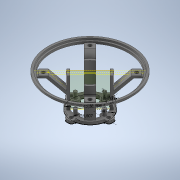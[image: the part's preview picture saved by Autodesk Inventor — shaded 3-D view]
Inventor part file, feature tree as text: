
AUTODESK INVENTOR PART (.ipt)
format: ipt  version: 2020 (Build 240168000, 168)  size: 594,432 bytes
history: native  units: mm
features: projected_geometry x28, sketch x16, extrude x9, other x5, pattern_circular x1, sweep x1
ambient origin geometry x8: Origin, YZ Plane, XZ Plane, XY Plane, X Axis, Y Axis, Z Axis, Center Point
bodies: Body1 (feature_tree)
feature tree (60):
  other  "Твердое тело1"
  sketch  "Эскиз1"
  extrude  "Выдавливание1"  Depth=44.0mm
  extrude  "Выдавливание2"  Depth=4.0mm
  sketch  "Эскиз3"
  extrude  "Выдавливание4"  Depth=40.0mm TaperAngle=360.0deg
  pattern_circular  "Круговой массив1"  [2 undecoded]
  other  "РабПлоскость2"
  sketch  "Эскиз5"
  other  "РабПлоскость1"
  sketch  "Эскиз6"
  sketch  "Эскиз7"
  extrude  "Выдавливание6"  Depth=4.5mm
  sketch  "Эскиз8"
  extrude  "Выдавливание7"  Depth=3.0mm
  sketch  "Эскиз9"
  other  "РабПлоскость3"
  sketch  "Эскиз10"
  sweep  "Сдвиг1"
  extrude  "Выдавливание8"  Depth=1.0mm
  extrude  "Выдавливание9"  TaperAngle=45.0deg  [1 undecoded]
  sketch  "Эскиз14"
  other  "РабПлоскость4"
  sketch  "Эскиз15"
  extrude  "Выдавливание10"  TaperAngle=135.0deg  [1 undecoded]
  extrude  "Выдавливание11"  Depth=34.0mm
  sketch  "Эскиз2"
  sketch  "Эскиз4"
  projected_geometry  "Спроецированная петля1"
  projected_geometry  "Спроецированная петля2"
  projected_geometry  "Спроецированная петля3"
  projected_geometry  "Спроецированная петля4"
  projected_geometry  "Спроецированная петля5"
  projected_geometry  "Спроецированная петля6"
  projected_geometry  "Спроецированная петля7"
  projected_geometry  "Спроецированная петля8"
  projected_geometry  "Спроецированная петля9"
  projected_geometry  "Спроецированная петля10"
  projected_geometry  "Спроецированная петля11"
  projected_geometry  "Спроецированная петля12"
  projected_geometry  "Спроецированная петля13"
  projected_geometry  "Спроецированная петля14"
  projected_geometry  "Спроецированная петля15"
  projected_geometry  "Спроецированная петля16"
  projected_geometry  "Спроецированная петля17"
  projected_geometry  "Спроецированная петля18"
  projected_geometry  "Спроецированная петля19"
  projected_geometry  "Спроецированная петля20"
  sketch  "Эскиз11"
  projected_geometry  "Спроецированная петля21"
  projected_geometry  "Спроецированная петля22"
  projected_geometry  "Спроецированная петля23"
  sketch  "3D эскиз1"
  sketch  "Эскиз12"
  sketch  "Эскиз13"
  projected_geometry  "Спроецированная петля24"
  projected_geometry  "Спроецированная петля25"
  projected_geometry  "Спроецированная петля26"
  projected_geometry  "Спроецированная петля27"
  projected_geometry  "Спроецированная петля28"
note: 4 required parameter values undecoded (feature->parameter linkage not recoverable at this tier; creation-order binding heuristic only, values carry confidence <= 0.55)
